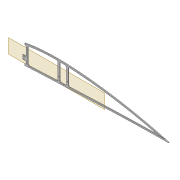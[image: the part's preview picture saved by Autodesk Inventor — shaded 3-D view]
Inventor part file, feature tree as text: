
AUTODESK INVENTOR PART (.ipt)
format: ipt  version: 2022 (Build 260153000, 153)  size: 585,216 bytes
history: native  units: mm
features: projected_geometry x11, sketch x9, extrude x8, shell x1, fillet x1, plane x1, chamfer x1
ambient origin geometry x8: Origin, YZ Plane, XZ Plane, XY Plane, X Axis, Y Axis, Z Axis, Center Point
bodies: Solid1 (feature_tree)
feature tree (32):
  extrude  "Extrusion1"  Depth=4.0mm
  shell  "Shell1"  Thickness=2.0mm
  extrude  "Extrusion8"  Depth=5.9mm
  extrude  "Extrusion3"  Depth=10.0mm TaperAngle=0.0deg
  extrude  "Extrusion4"  Depth=2.0mm
  fillet  "Fillet1"  Radius=5.0mm
  sketch  "Sketch10"  dims[d22=2.0mm d23=0.0mm d31=2.0mm d32=5.0mm]
  extrude  "Extrusion5"  Depth=2.5mm
  plane  "Work Plane2"
  extrude  "Extrusion9"  Depth=1.6mm
  extrude  "Extrusion10"  Depth=80.0mm
  chamfer  "Chamfer1"  Distance=2.0mm
  extrude  "Extrusion12"  Depth=12.0mm
  sketch  "Sketch29"  dims[d63=6.0mm d64=2.0mm d65=0.0mm]
  sketch  "Sketch30"  dims[d66=3.0mm d67=12.0mm d68=5.0mm d69=10.0mm d70=12.0mm d71=3.05mm d72=10.0mm d73=0.0mm d75=100.0mm d76=20.0mm d78=10.0mm d79=0.0mm d82=3.0mm d83=2.0mm d84=45.0deg d85=1.0mm d86=1.0mm d87=1.0mm d88=1.0mm d89=1.0mm d90=1.0mm d91=10.0mm d92=0.0mm d93=0.5mm]
  sketch  "Sketch3"  dims[d0=2.0mm d1=0.0mm d2=4.0mm d7=2.0mm]
  sketch  "Sketch8"  dims[d8=2.0mm d9=5.9mm]
  sketch  "Sketch9"  dims[d13=10.0mm d14=0.0mm d16=10.0mm d17=0.0mm]
  projected_geometry  "Projected Loop4"
  projected_geometry  "Projected Loop10"
  sketch  "Sketch24"  dims[d34=1.6mm d35=2.5mm]
  projected_geometry  "Projected Loop11"
  projected_geometry  "Projected Loop12"
  projected_geometry  "Projected Loop13"
  sketch  "Sketch26"  dims[d37=5.0mm d38=1.6mm]
  projected_geometry  "Projected Loop14"
  sketch  "Sketch28"  dims[d40=2.5mm d62=80.0mm]
  projected_geometry  "Project Cut Edges1"
  projected_geometry  "Project Cut Edges2"
  projected_geometry  "Project Cut Edges3"
  projected_geometry  "Project Cut Edges4"
  projected_geometry  "Project Cut Edges5"
